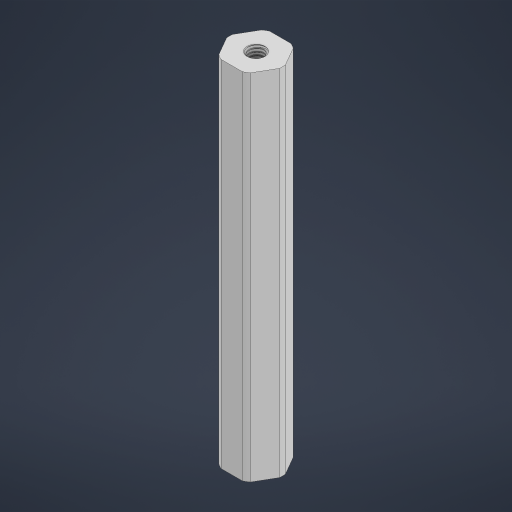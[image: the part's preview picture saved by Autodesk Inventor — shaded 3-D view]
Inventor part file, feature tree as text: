
AUTODESK INVENTOR PART (.ipt)
format: ipt  version: 2023 (Build 270158000, 158)  size: 1,020,928 bytes
history: native  units: in
note: dims shown in document units (in); Inventor stores cm internally (conversion verified against a paired STEP export)
features: mirror x1
ambient origin geometry x8: Origin, YZ Plane, XZ Plane, XY Plane, X Axis, Y Axis, Z Axis, Center Point
bodies: Solid1 (feature_tree)
feature tree (1):
  mirror  "Mirror2"
